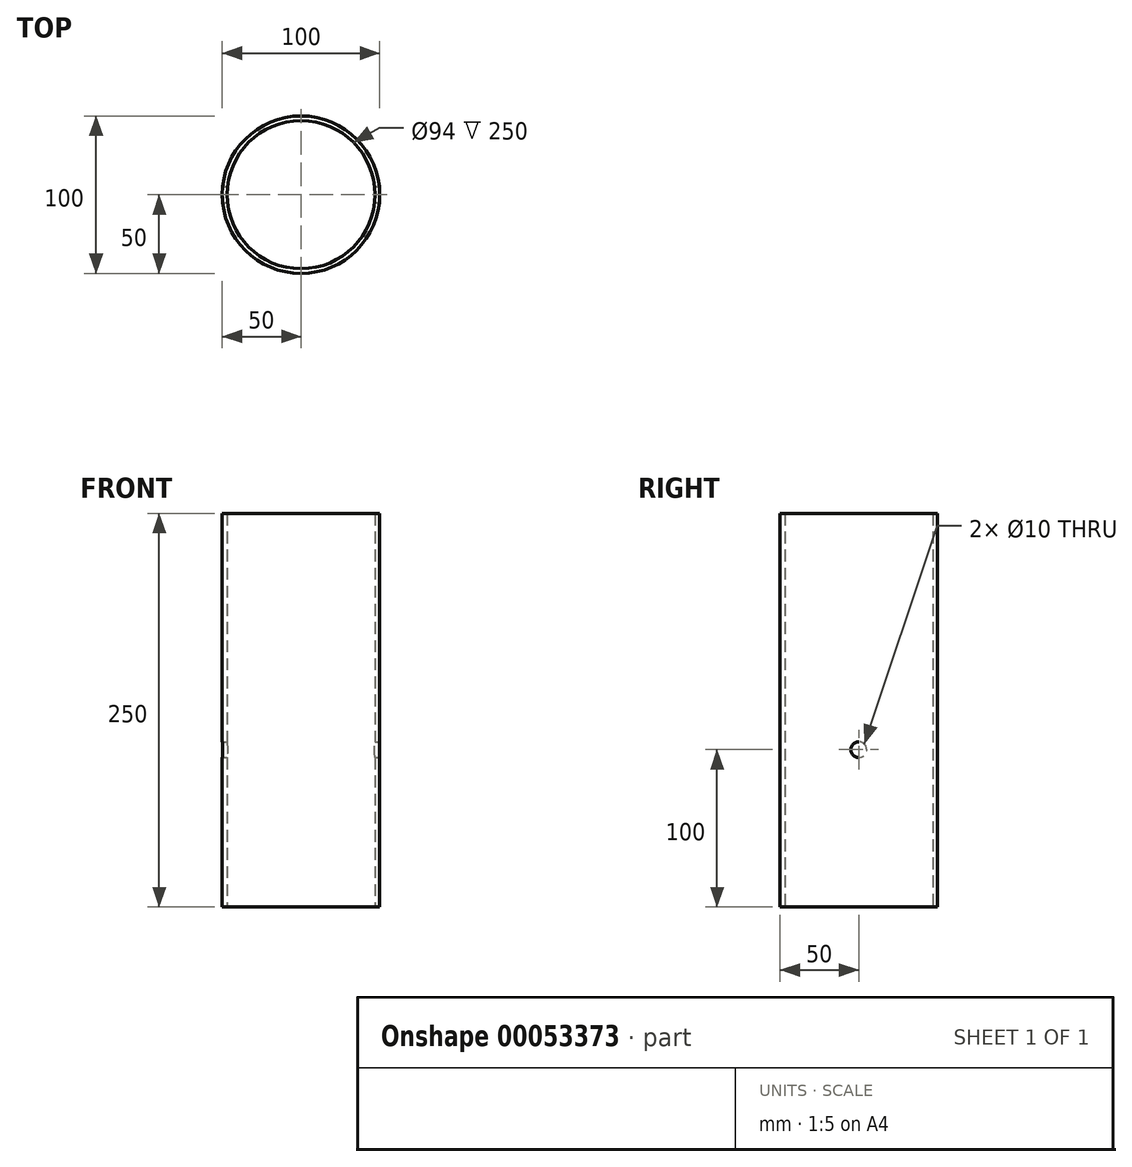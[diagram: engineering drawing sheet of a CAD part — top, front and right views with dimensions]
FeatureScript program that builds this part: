
annotation { "Feature Type Name" : "Feature", "Feature Type Description" : "" }
export const myFeature = defineFeature(function(context is Context, id is Id, definition is map)
    precondition{}
    {
        {
            var Q0;
            Q0=qCreatedBy(makeId("Top.planeOp"),FACE);
            var sketch = newSketch(context, id + "F0", { "sketchPlane" : qUnion([Q0])});
            skCircle(sketch, "E0", {"center": v(0, 0) * mm, "radius": 50 * mm});
            skCircle(sketch, "E1", {"center": v(0, 0) * mm, "radius": 47 * mm});
            skSolve(sketch);
        }
        {
            var Q0;
            Q0=qSketchRegion(id+"F0",true);
            extrude(context, id + "F1", {"entities" : qUnion([Q0]), "depth" : 250 * mm});
        }
        {
            var Q0;
            Q0=qCreatedBy(makeId("Right.planeOp"),FACE);
            var sketch = newSketch(context, id + "F2", { "sketchPlane" : qUnion([Q0])});
            skCircle(sketch, "E2", {"center": v(0, 100) * mm, "radius": 5 * mm});
            skSolve(sketch);
        }
        {
            var Q0;
            Q0=qSketchRegion(id+"F2",true);
            extrude(context, id + "F3", {"entities" : qUnion([Q0]), "operationType" : NewBodyOperationType.REMOVE, "endBound" : BoundingType.SYMMETRIC, "oppositeDirection" : true, "depth" : 200 * mm});
        }
    });
